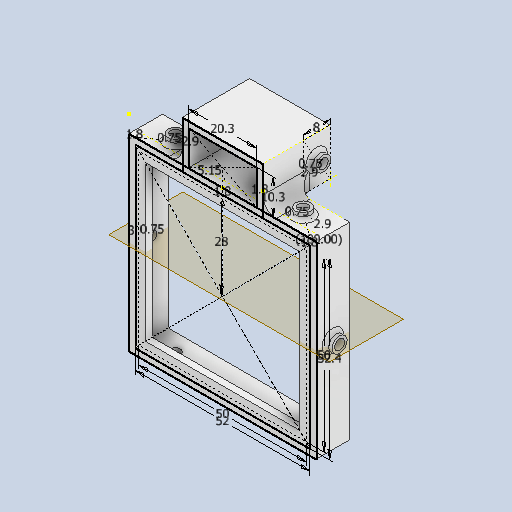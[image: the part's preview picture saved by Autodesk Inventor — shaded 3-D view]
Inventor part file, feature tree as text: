
AUTODESK INVENTOR PART (.ipt)
format: ipt  version: 2023 (Build 270158000, 158)  size: 308,736 bytes
history: native  units: mm
features: extrude x9, sketch x5, fillet x4, mirror x2, plane x1
ambient origin geometry x8: Origin, YZ Plane, XZ Plane, XY Plane, X Axis, Y Axis, Z Axis, Center Point
bodies: Solid1 (feature_tree)
feature tree (21):
  sketch  "Sketch1"  dims[d0=5.15mm d1=28.0mm]
  extrude  "Extrusion1"  Depth=28.0mm
  extrude  "Extrusion2"  Depth=50.0mm
  extrude  "Extrusion3"  Depth=52.4mm
  sketch  "Sketch3"  dims[d4=52.0mm d5=52.4mm]
  extrude  "Extrusion4"  Depth=10.3mm
  fillet  "Fillet1"  Radius=1.8mm
  extrude  "Extrusion5"  Depth=1.0mm TaperAngle=0.0deg
  mirror  "Mirror1"
  sketch  "Sketch4"  dims[d6=20.3mm d7=10.3mm d8=1.8mm]
  extrude  "Extrusion6"  Depth=10.0mm TaperAngle=0.0deg
  extrude  "Extrusion7"  Depth=1.0mm
  fillet  "Fillet2"  Radius=2.0mm
  plane  "Work Plane1"
  mirror  "Mirror2"
  fillet  "Fillet3"  Radius=3.0mm
  sketch  "Sketch5"  dims[d9=1.8mm d10=20.0mm d11=0.0mm d12=10.0mm d13=0.0mm d14=5.0mm d15=2.0mm d16=0.0mm d17=3.0mm d18=0.75mm d19=2.0mm d20=0.0mm d21=1.0mm d22=2.0mm d23=0.0mm d24=1.8mm d25=2.9mm d26=0.75mm d27=1.8mm d28=180.0deg d29=2.9mm d30=0.75mm d31=2.0mm d32=0.0mm d33=2.0mm d34=0.0mm d35=1.0mm d36=4.0mm d37=8.0mm d38=2.9mm d39=0.75mm d40=2.0mm d41=0.0mm d42=2.0mm d43=0.0mm d44=1.0mm]
  extrude  "Extrusion8"  Depth=1.0mm
  extrude  "Extrusion9"  Depth=1.0mm TaperAngle=0.0deg
  fillet  "Fillet4"  Radius=1.0mm
  sketch  "Sketch2"  dims[d2=50.0mm d3=50.0mm]
